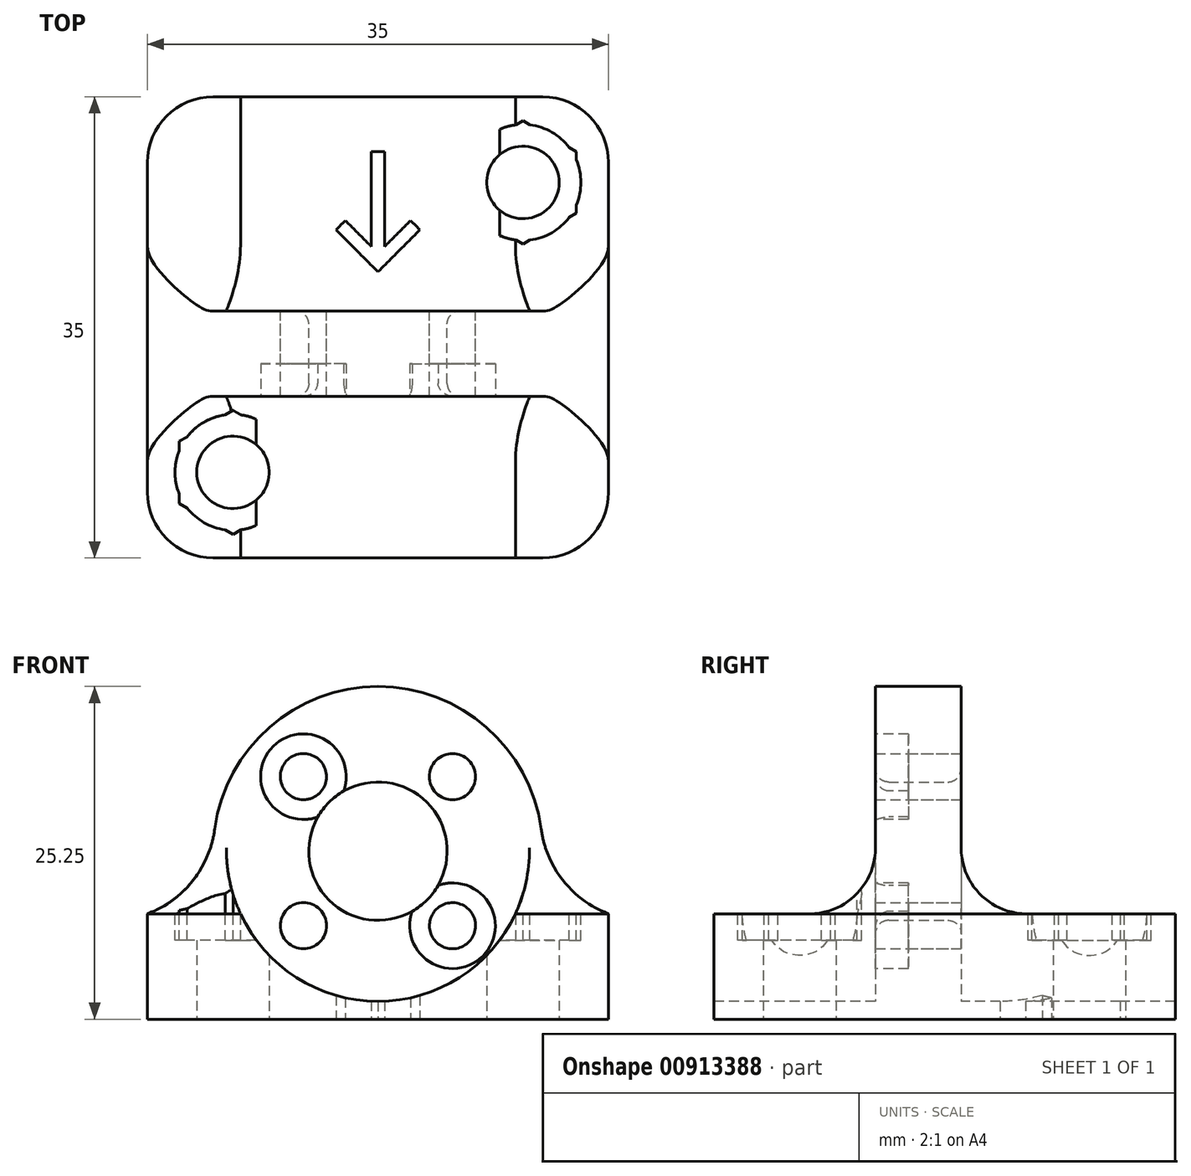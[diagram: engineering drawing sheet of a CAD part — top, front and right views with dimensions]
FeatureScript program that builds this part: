
annotation { "Feature Type Name" : "Feature", "Feature Type Description" : "" }
export const myFeature = defineFeature(function(context is Context, id is Id, definition is map)
    precondition{}
    {
        {
            var Q0;
            Q0=qCreatedBy(makeId("Front.planeOp"),FACE);
            cPlane(context, id + "F0", {"entities" : qUnion([Q0]), "cplaneType" : CPlaneType.OFFSET, "offset" : 2 * mm, "width" : 150 * mm, "height" : 150 * mm});
        }
        {
            var Q0;
            Q0=qCreatedBy(makeId("Top.planeOp"),FACE);
            var sketch = newSketch(context, id + "F1", { "sketchPlane" : qUnion([Q0])});
            skLineSegment(sketch, "E0.bottom", {"start": v(-17.5, 17.5) * mm, "end": v(17.5, 17.5) * mm});
            skLineSegment(sketch, "E0.top", {"start": v(-17.5, -17.5) * mm, "end": v(17.5, -17.5) * mm});
            skLineSegment(sketch, "E0.left", {"start": v(-17.5, 17.5) * mm, "end": v(-17.5, -17.5) * mm});
            skLineSegment(sketch, "E0.right", {"start": v(17.5, 17.5) * mm, "end": v(17.5, -17.5) * mm});
            skPoint(sketch, "E0.middle", {"position": v(0, 0) * mm});
            skLineSegment(sketch, "E1.bottom", {"start": v(-11, 11) * mm, "end": v(11, 11) * mm, "construction": true});
            skLineSegment(sketch, "E1.top", {"start": v(-11, -11) * mm, "end": v(11, -11) * mm, "construction": true});
            skLineSegment(sketch, "E1.left", {"start": v(-11, 11) * mm, "end": v(-11, -11) * mm, "construction": true});
            skLineSegment(sketch, "E1.right", {"start": v(11, 11) * mm, "end": v(11, -11) * mm, "construction": true});
            skCircle(sketch, "E2", {"center": v(-11, 11) * mm, "radius": 2.75 * mm, "construction": true});
            skCircle(sketch, "E3", {"center": v(11, 11) * mm, "radius": 2.75 * mm});
            skCircle(sketch, "E4", {"center": v(11, -11) * mm, "radius": 2.75 * mm, "construction": true});
            skCircle(sketch, "E5", {"center": v(-11, -11) * mm, "radius": 2.75 * mm});
            skSolve(sketch);
        }
        {
            var Q0;
            Q0=qSketchRegion(id+"F1",true);
            extrude(context, id + "F2", {"entities" : qUnion([Q0]), "depth" : 8 * mm, "offsetDistance" : 25 * mm});
        }
        {
            var Q0;
            Q0=qCreatedBy(id+"F0.planeOp",FACE);
            var sketch = newSketch(context, id + "F3", { "sketchPlane" : qUnion([Q0])});
            skLineSegment(sketch, "E6", {"start": v(0, 0) * mm, "end": v(0, 12.75) * mm, "construction": true});
            skArc(sketch, "E7", {"start": v(12.5, 12.75) * mm, "mid": v(0, 25.25) * mm, "end": v(-12.5, 12.75) * mm});
            skLineSegment(sketch, "E8", {"start": v(-12.5, 12.75) * mm, "end": v(-12.5, 0) * mm});
            skLineSegment(sketch, "E9.MirrorCS", {"start": v(12.5, 12.75) * mm, "end": v(12.5, 0) * mm});
            skCircle(sketch, "E10", {"center": v(0, 12.75) * mm, "radius": 5.25 * mm});
            skCircle(sketch, "E11", {"center": v(0, 12.75) * mm, "radius": 8 * mm, "construction": true});
            skLineSegment(sketch, "E12", {"start": v(0, 20.75) * mm, "end": v(0, 4.75) * mm, "construction": true});
            skPoint(sketch, "E12.startSnap0", {"position": v(0, 25.25) * mm});
            skLineSegment(sketch, "E13", {"start": v(-8, 12.75) * mm, "end": v(8, 12.75) * mm, "construction": true});
            skLineSegment(sketch, "E14", {"start": v(0, 12.75) * mm, "end": v(-5.66, 18.4) * mm, "construction": true});
            skLineSegment(sketch, "E15", {"start": v(0, 12.75) * mm, "end": v(-5.66, 7.1) * mm, "construction": true});
            skLineSegment(sketch, "E16.MirrorCS", {"start": v(0, 12.75) * mm, "end": v(5.66, 18.4) * mm, "construction": true});
            skLineSegment(sketch, "E17.MirrorCS", {"start": v(0, 12.75) * mm, "end": v(5.66, 7.1) * mm, "construction": true});
            skCircle(sketch, "E18", {"center": v(-5.66, 18.4) * mm, "radius": 1.75 * mm});
            skCircle(sketch, "E19", {"center": v(-5.66, 7.1) * mm, "radius": 1.75 * mm});
            skCircle(sketch, "E20", {"center": v(5.66, 7.1) * mm, "radius": 1.75 * mm});
            skCircle(sketch, "E21", {"center": v(5.66, 18.4) * mm, "radius": 1.75 * mm});
            skLineSegment(sketch, "E22", {"start": v(-12.5, 0) * mm, "end": v(12.5, 0) * mm});
            skSolve(sketch);
        }
        {
            var Q0;
            Q0=qCreatedBy(makeId("Front.planeOp"),FACE);
            var sketch = newSketch(context, id + "F4", { "sketchPlane" : qUnion([Q0])});
            skLineSegment(sketch, "E23", {"start": v(0, 0) * mm, "end": v(0, 12.85) * mm, "construction": true});
            skCircle(sketch, "E24", {"center": v(0, 12.85) * mm, "radius": 11.5 * mm});
            skSolve(sketch);
        }
        {
            var Q0;
            Q0=qSketchRegion(id+"F4",true);
            extrude(context, id + "F5", {"entities" : qUnion([Q0]), "operationType" : NewBodyOperationType.REMOVE, "oppositeDirection" : true, "depth" : 36 * mm, "offsetDistance" : 25 * mm, "symmetric" : true});
        }
        {
            var Q0;
            Q0=qSketchRegion(id+"F3",true);
            extrude(context, id + "F6", {"entities" : qUnion([Q0]), "operationType" : NewBodyOperationType.ADD, "depth" : 6.5 * mm, "offsetDistance" : 25 * mm, "symmetric" : true});
        }
        {
            var Q0;
            {var subQ0=sQuery(id+"F1.wireOp",EDGE,"E4");var subQ1=sQuery(id+"F1.wireOp",EDGE,"E0.top");var subQ2=sQuery(id+"F1.wireOp",EDGE,"E0.right");var subQ3=sQuery(id+"F1.wireOp",EDGE,"E0.bottom");Q0=makeQuery(id+"F6.boolean.opBoolean","INTERSECT",EDGE,{"derivedFrom":[makeQuery(id+"F5.boolean.opBoolean","SPLIT",FACE,{"disambiguationData":[TD([makeQuery(id+"F2.opExtrude","SWEPT_FACE",FACE,{"disambiguationData":[OSD([subQ2])]})])],"derivedFrom":makeQuery(id+"F2.opExtrude","CAP_FACE",FACE,{"disambiguationData":[OSD([subQ3,subQ1,sQuery(id+"F1.wireOp",EDGE,"E0.left"),subQ2,sQuery(id+"F1.wireOp",EDGE,"E2"),subQ0])],"isStart":false})}),makeQuery(id+"F6.opExtrude","SWEPT_FACE",FACE,{"disambiguationData":[OSD([sQuery(id+"F3.wireOp",EDGE,"E9.MirrorCS")])]})]});}
            var Q1;
            {var subQ0=sQuery(id+"F1.wireOp",EDGE,"E2");var subQ1=sQuery(id+"F1.wireOp",EDGE,"E0.left");var subQ2=sQuery(id+"F1.wireOp",EDGE,"E0.top");var subQ3=sQuery(id+"F1.wireOp",EDGE,"E0.bottom");Q1=makeQuery(id+"F6.boolean.opBoolean","INTERSECT",EDGE,{"derivedFrom":[makeQuery(id+"F5.boolean.opBoolean","SPLIT",FACE,{"disambiguationData":[TD([makeQuery(id+"F2.opExtrude","SWEPT_FACE",FACE,{"disambiguationData":[OSD([subQ1])]})])],"derivedFrom":makeQuery(id+"F2.opExtrude","CAP_FACE",FACE,{"disambiguationData":[OSD([subQ3,subQ2,subQ1,sQuery(id+"F1.wireOp",EDGE,"E0.right"),subQ0,sQuery(id+"F1.wireOp",EDGE,"E4")])],"isStart":false})}),makeQuery(id+"F6.opExtrude","SWEPT_FACE",FACE,{"disambiguationData":[OSD([sQuery(id+"F3.wireOp",EDGE,"E8")])]})]});}
            fillet(context, id + "F7", {"entities" : qUnion([Q0, Q1]), "radius" : 8 * mm, "tangentPropagation" : true, "allowEdgeOverflow" : false});
        }
        {
            var Q0;
            {var subQ0=sQuery(id+"F1.wireOp",EDGE,"E2");var subQ1=sQuery(id+"F1.wireOp",EDGE,"E0.left");var subQ2=sQuery(id+"F1.wireOp",EDGE,"E0.top");var subQ3=sQuery(id+"F1.wireOp",EDGE,"E0.bottom");Q0=makeQuery(id+"F7.opFillet","SPLIT",FACE,{"disambiguationData":[OD(0.0)],"derivedFrom":makeQuery(id+"F5.boolean.opBoolean","SPLIT",FACE,{"disambiguationData":[TD([makeQuery(id+"F2.opExtrude","SWEPT_FACE",FACE,{"disambiguationData":[OSD([subQ1])]})])],"derivedFrom":makeQuery(id+"F2.opExtrude","CAP_FACE",FACE,{"disambiguationData":[OSD([subQ3,subQ2,subQ1,sQuery(id+"F1.wireOp",EDGE,"E0.right"),subQ0,sQuery(id+"F1.wireOp",EDGE,"E4")])],"isStart":false})})});}
            var sketch = newSketch(context, id + "F8", { "sketchPlane" : qUnion([Q0])});
            skPoint(sketch, "E25.0.midPoint.positionSnap0", {"position": v(5.2, -11) * mm});
            skLineSegment(sketch, "E26", {"start": v(17.5, 17.5) * mm, "end": v(-17.5, -17.5) * mm, "construction": true});
            skCircle(sketch, "E27.cCircle", {"center": v(11, 11) * mm, "radius": 4.05 * mm, "construction": true});
            skLineSegment(sketch, "E27.0", {"start": v(15.05, 13.34) * mm, "end": v(15.05, 8.66) * mm});
            skLineSegment(sketch, "E27.1", {"start": v(15.05, 8.66) * mm, "end": v(11, 6.32) * mm});
            skLineSegment(sketch, "E27.2", {"start": v(11, 6.32) * mm, "end": v(6.95, 8.66) * mm});
            skLineSegment(sketch, "E27.3", {"start": v(6.95, 8.66) * mm, "end": v(6.95, 13.34) * mm});
            skLineSegment(sketch, "E27.4", {"start": v(6.95, 13.34) * mm, "end": v(11, 15.68) * mm});
            skLineSegment(sketch, "E27.5", {"start": v(11, 15.68) * mm, "end": v(15.05, 13.34) * mm});
            skPoint(sketch, "E27.0.midPoint", {"position": v(15.05, 11) * mm});
            skCircle(sketch, "E28.cCircle", {"center": v(-11, -11) * mm, "radius": 4.08 * mm, "construction": true});
            skLineSegment(sketch, "E28.0", {"start": v(-11, -6.3) * mm, "end": v(-6.93, -8.65) * mm});
            skLineSegment(sketch, "E28.1", {"start": v(-6.93, -8.65) * mm, "end": v(-6.93, -13.35) * mm});
            skLineSegment(sketch, "E28.2", {"start": v(-6.93, -13.35) * mm, "end": v(-11, -15.7) * mm});
            skLineSegment(sketch, "E28.3", {"start": v(-11, -15.7) * mm, "end": v(-15.08, -13.35) * mm});
            skLineSegment(sketch, "E28.4", {"start": v(-15.07, -13.35) * mm, "end": v(-15.07, -8.65) * mm});
            skLineSegment(sketch, "E28.5", {"start": v(-15.07, -8.65) * mm, "end": v(-11, -6.3) * mm});
            skPoint(sketch, "E28.0.midPoint", {"position": v(-8.96, -7.47) * mm});
            skSolve(sketch);
        }
        {
            var Q0;
            Q0=qSketchRegion(id+"F8",true);
            extrude(context, id + "F9", {"entities" : qUnion([Q0]), "operationType" : NewBodyOperationType.REMOVE, "oppositeDirection" : true, "depth" : 2 * mm, "offsetDistance" : 25 * mm});
        }
        {
            var Q0;
            {var subQ0=sQuery(id+"F1.wireOp",EDGE,"E2");var subQ1=sQuery(id+"F1.wireOp",EDGE,"E0.left");var subQ2=sQuery(id+"F1.wireOp",EDGE,"E0.top");var subQ3=sQuery(id+"F1.wireOp",EDGE,"E0.bottom");Q0=makeQuery(id+"F7.opFillet","SPLIT",FACE,{"disambiguationData":[OD(0.0)],"derivedFrom":makeQuery(id+"F5.boolean.opBoolean","SPLIT",FACE,{"disambiguationData":[TD([makeQuery(id+"F2.opExtrude","SWEPT_FACE",FACE,{"disambiguationData":[OSD([subQ1])]})])],"derivedFrom":makeQuery(id+"F2.opExtrude","CAP_FACE",FACE,{"disambiguationData":[OSD([subQ3,subQ2,subQ1,sQuery(id+"F1.wireOp",EDGE,"E0.right"),subQ0,sQuery(id+"F1.wireOp",EDGE,"E4")])],"isStart":false})})});}
            var sketch = newSketch(context, id + "F10", { "sketchPlane" : qUnion([Q0])});
            skCircle(sketch, "E29", {"center": v(11, 11) * mm, "radius": 4.4 * mm});
            skCircle(sketch, "E30", {"center": v(-11, -11) * mm, "radius": 4.4 * mm});
            skSolve(sketch);
        }
        {
            var Q0;
            Q0=qSketchRegion(id+"F10",true);
            extrude(context, id + "F11", {"entities" : qUnion([Q0]), "operationType" : NewBodyOperationType.REMOVE, "oppositeDirection" : true, "depth" : 2 * mm, "offsetDistance" : 25 * mm});
        }
        {
            var Q0;
            {var subQ0=sQuery(id+"F1.wireOp",EDGE,"E4");var subQ1=sQuery(id+"F1.wireOp",EDGE,"E0.top");var subQ2=sQuery(id+"F1.wireOp",EDGE,"E0.right");var subQ3=sQuery(id+"F1.wireOp",EDGE,"E0.bottom");Q0=makeQuery(id+"F6.boolean.opBoolean","INTERSECT",EDGE,{"derivedFrom":[makeQuery(id+"F5.boolean.opBoolean","SPLIT",FACE,{"disambiguationData":[TD([makeQuery(id+"F2.opExtrude","SWEPT_FACE",FACE,{"disambiguationData":[OSD([subQ2])]})])],"derivedFrom":makeQuery(id+"F2.opExtrude","CAP_FACE",FACE,{"disambiguationData":[OSD([subQ3,subQ1,sQuery(id+"F1.wireOp",EDGE,"E0.left"),subQ2,sQuery(id+"F1.wireOp",EDGE,"E2"),subQ0])],"isStart":false})}),makeQuery(id+"F6.opExtrude","CAP_FACE",FACE,{"disambiguationData":[OSD([sQuery(id+"F3.wireOp",EDGE,"E7"),sQuery(id+"F3.wireOp",EDGE,"E8"),sQuery(id+"F3.wireOp",EDGE,"E9.MirrorCS"),sQuery(id+"F3.wireOp",EDGE,"E10"),sQuery(id+"F3.wireOp",EDGE,"E18"),sQuery(id+"F3.wireOp",EDGE,"E19"),sQuery(id+"F3.wireOp",EDGE,"E20"),sQuery(id+"F3.wireOp",EDGE,"E21"),sQuery(id+"F3.wireOp",EDGE,"E22")])],"isStart":true})]});}
            var Q1;
            {var subQ0=sQuery(id+"F1.wireOp",EDGE,"E2");var subQ1=sQuery(id+"F1.wireOp",EDGE,"E0.left");var subQ2=sQuery(id+"F1.wireOp",EDGE,"E0.top");var subQ3=sQuery(id+"F1.wireOp",EDGE,"E0.bottom");Q1=makeQuery(id+"F6.boolean.opBoolean","INTERSECT",EDGE,{"derivedFrom":[makeQuery(id+"F5.boolean.opBoolean","SPLIT",FACE,{"disambiguationData":[TD([makeQuery(id+"F2.opExtrude","SWEPT_FACE",FACE,{"disambiguationData":[OSD([subQ1])]})])],"derivedFrom":makeQuery(id+"F2.opExtrude","CAP_FACE",FACE,{"disambiguationData":[OSD([subQ3,subQ2,subQ1,sQuery(id+"F1.wireOp",EDGE,"E0.right"),subQ0,sQuery(id+"F1.wireOp",EDGE,"E4")])],"isStart":false})}),makeQuery(id+"F6.opExtrude","CAP_FACE",FACE,{"disambiguationData":[OSD([sQuery(id+"F3.wireOp",EDGE,"E7"),sQuery(id+"F3.wireOp",EDGE,"E8"),sQuery(id+"F3.wireOp",EDGE,"E9.MirrorCS"),sQuery(id+"F3.wireOp",EDGE,"E10"),sQuery(id+"F3.wireOp",EDGE,"E18"),sQuery(id+"F3.wireOp",EDGE,"E19"),sQuery(id+"F3.wireOp",EDGE,"E20"),sQuery(id+"F3.wireOp",EDGE,"E21"),sQuery(id+"F3.wireOp",EDGE,"E22")])],"isStart":true})]});}
            var Q2;
            {var subQ0=sQuery(id+"F1.wireOp",EDGE,"E2");var subQ1=sQuery(id+"F1.wireOp",EDGE,"E0.left");var subQ2=sQuery(id+"F1.wireOp",EDGE,"E0.top");var subQ3=sQuery(id+"F1.wireOp",EDGE,"E0.bottom");Q2=makeQuery(id+"F6.boolean.opBoolean","INTERSECT",EDGE,{"derivedFrom":[makeQuery(id+"F5.boolean.opBoolean","SPLIT",FACE,{"disambiguationData":[TD([makeQuery(id+"F2.opExtrude","SWEPT_FACE",FACE,{"disambiguationData":[OSD([subQ1])]})])],"derivedFrom":makeQuery(id+"F2.opExtrude","CAP_FACE",FACE,{"disambiguationData":[OSD([subQ3,subQ2,subQ1,sQuery(id+"F1.wireOp",EDGE,"E0.right"),subQ0,sQuery(id+"F1.wireOp",EDGE,"E4")])],"isStart":false})}),makeQuery(id+"F6.opExtrude","CAP_FACE",FACE,{"disambiguationData":[OSD([sQuery(id+"F3.wireOp",EDGE,"E7"),sQuery(id+"F3.wireOp",EDGE,"E8"),sQuery(id+"F3.wireOp",EDGE,"E9.MirrorCS"),sQuery(id+"F3.wireOp",EDGE,"E10"),sQuery(id+"F3.wireOp",EDGE,"E18"),sQuery(id+"F3.wireOp",EDGE,"E19"),sQuery(id+"F3.wireOp",EDGE,"E20"),sQuery(id+"F3.wireOp",EDGE,"E21"),sQuery(id+"F3.wireOp",EDGE,"E22")])],"isStart":false})]});}
            var Q3;
            {var subQ0=sQuery(id+"F1.wireOp",EDGE,"E4");var subQ1=sQuery(id+"F1.wireOp",EDGE,"E0.top");var subQ2=sQuery(id+"F1.wireOp",EDGE,"E0.right");var subQ3=sQuery(id+"F1.wireOp",EDGE,"E0.bottom");Q3=makeQuery(id+"F6.boolean.opBoolean","INTERSECT",EDGE,{"derivedFrom":[makeQuery(id+"F5.boolean.opBoolean","SPLIT",FACE,{"disambiguationData":[TD([makeQuery(id+"F2.opExtrude","SWEPT_FACE",FACE,{"disambiguationData":[OSD([subQ2])]})])],"derivedFrom":makeQuery(id+"F2.opExtrude","CAP_FACE",FACE,{"disambiguationData":[OSD([subQ3,subQ1,sQuery(id+"F1.wireOp",EDGE,"E0.left"),subQ2,sQuery(id+"F1.wireOp",EDGE,"E2"),subQ0])],"isStart":false})}),makeQuery(id+"F6.opExtrude","CAP_FACE",FACE,{"disambiguationData":[OSD([sQuery(id+"F3.wireOp",EDGE,"E7"),sQuery(id+"F3.wireOp",EDGE,"E8"),sQuery(id+"F3.wireOp",EDGE,"E9.MirrorCS"),sQuery(id+"F3.wireOp",EDGE,"E10"),sQuery(id+"F3.wireOp",EDGE,"E18"),sQuery(id+"F3.wireOp",EDGE,"E19"),sQuery(id+"F3.wireOp",EDGE,"E20"),sQuery(id+"F3.wireOp",EDGE,"E21"),sQuery(id+"F3.wireOp",EDGE,"E22")])],"isStart":false})]});}
            var Q4;
            Q4=makeQuery(id+"F2.opExtrude","SWEPT_EDGE",EDGE,{"disambiguationData":[OSD([sQuery(id+"F1.wireOp",EDGE,"E0.top"),sQuery(id+"F1.wireOp",EDGE,"E0.left")])]});
            var Q5;
            Q5=makeQuery(id+"F2.opExtrude","SWEPT_EDGE",EDGE,{"disambiguationData":[OSD([sQuery(id+"F1.wireOp",EDGE,"E0.bottom"),sQuery(id+"F1.wireOp",EDGE,"E0.left")])]});
            var Q6;
            Q6=makeQuery(id+"F2.opExtrude","SWEPT_EDGE",EDGE,{"disambiguationData":[OSD([sQuery(id+"F1.wireOp",EDGE,"E0.bottom"),sQuery(id+"F1.wireOp",EDGE,"E0.right")])]});
            var Q7;
            Q7=makeQuery(id+"F2.opExtrude","SWEPT_EDGE",EDGE,{"disambiguationData":[OSD([sQuery(id+"F1.wireOp",EDGE,"E0.top"),sQuery(id+"F1.wireOp",EDGE,"E0.right")])]});
            fillet(context, id + "F12", {"entities" : qUnion([Q0, Q1, Q2, Q3, Q4, Q5, Q6, Q7]), "radius" : 5 * mm, "tangentPropagation" : true, "allowEdgeOverflow" : false});
        }
        {
            var Q0;
            Q0=makeQuery(id+"F6.opExtrude","CAP_FACE",FACE,{"disambiguationData":[OSD([sQuery(id+"F3.wireOp",EDGE,"E7"),sQuery(id+"F3.wireOp",EDGE,"E8"),sQuery(id+"F3.wireOp",EDGE,"E9.MirrorCS"),sQuery(id+"F3.wireOp",EDGE,"E10"),sQuery(id+"F3.wireOp",EDGE,"E18"),sQuery(id+"F3.wireOp",EDGE,"E20"),sQuery(id+"F3.wireOp",EDGE,"E22")])],"isStart":false});
            var sketch = newSketch(context, id + "F13", { "sketchPlane" : qUnion([Q0])});
            skCircle(sketch, "E31", {"center": v(-5.66, 18.4) * mm, "radius": 3.25 * mm});
            skCircle(sketch, "E32", {"center": v(5.66, 7.1) * mm, "radius": 3.25 * mm});
            skLineSegment(sketch, "E33", {"start": v(0, 12.75) * mm, "end": v(12.71, 12.75) * mm, "construction": true});
            skCircle(sketch, "E34.MirrorC", {"center": v(5.66, 18.4) * mm, "radius": 3.25 * mm});
            skCircle(sketch, "E35.MirrorC", {"center": v(-5.66, 7.1) * mm, "radius": 3.25 * mm});
            skSolve(sketch);
        }
        {
            var Q0;
            Q0=makeQuery(id+"F13.imprint","IMPRINT",FACE,{"disambiguationData":[TD([[makeQuery(id+"F13.imprint","IMPRINT",EDGE,{"derivedFrom":sQuery(id+"F13.wireOp",EDGE,"E31")}),1.0]])]});
            var Q1;
            Q1=makeQuery(id+"F13.imprint","IMPRINT",FACE,{"disambiguationData":[TD([[makeQuery(id+"F13.imprint","IMPRINT",EDGE,{"derivedFrom":sQuery(id+"F13.wireOp",EDGE,"E32")}),1.0]])]});
            var Q2;
            Q2=makeQuery(id+"F13.imprint","IMPRINT",FACE,{"disambiguationData":[TD([[makeQuery(id+"F13.imprint","IMPRINT",EDGE,{"derivedFrom":makeQuery(id+"F6.opExtrude","CAP_EDGE",EDGE,{"disambiguationData":[OSD([sQuery(id+"F3.wireOp",EDGE,"E18")])],"isStart":false})}),-1.0]])]});
            var Q3;
            Q3=makeQuery(id+"F13.imprint","IMPRINT",FACE,{"disambiguationData":[TD([[makeQuery(id+"F13.imprint","IMPRINT",EDGE,{"derivedFrom":makeQuery(id+"F6.opExtrude","CAP_EDGE",EDGE,{"disambiguationData":[OSD([sQuery(id+"F3.wireOp",EDGE,"E20")])],"isStart":false})}),-1.0]])]});
            var Q4;
            {var subQ0=sQuery(id+"F13.wireOp",EDGE,"E34.MirrorC");var subQ1=makeQuery(id+"F6.opExtrude","CAP_EDGE",EDGE,{"disambiguationData":[OSD([sQuery(id+"F3.wireOp",EDGE,"E10")])],"isStart":false});var subQ2=makeQuery(id+"F13.imprint","INTERSECT",VERTEX,{"disambiguationData":[OD(0.0)],"derivedFrom":[subQ1,subQ0]});Q4=makeQuery(id+"F13.imprint","IMPRINT",FACE,{"disambiguationData":[TD([[makeQuery(id+"F13.imprint","IMPRINT",EDGE,{"disambiguationData":[TD([[subQ2,-1.0]])],"derivedFrom":subQ0}),-1.0]])]});}
            var Q5;
            {var subQ0=sQuery(id+"F13.wireOp",EDGE,"E35.MirrorC");var subQ1=makeQuery(id+"F6.opExtrude","CAP_EDGE",EDGE,{"disambiguationData":[OSD([sQuery(id+"F3.wireOp",EDGE,"E10")])],"isStart":false});var subQ2=makeQuery(id+"F13.imprint","INTERSECT",VERTEX,{"disambiguationData":[OD(0.0)],"derivedFrom":[subQ1,subQ0]});Q5=makeQuery(id+"F13.imprint","IMPRINT",FACE,{"disambiguationData":[TD([[makeQuery(id+"F13.imprint","IMPRINT",EDGE,{"disambiguationData":[TD([[subQ2,1.0]])],"derivedFrom":subQ0}),-1.0]])]});}
            var Q6;
            Q6=makeQuery(id+"F6.opExtrude","CAP_FACE",FACE,{"disambiguationData":[OSD([sQuery(id+"F3.wireOp",EDGE,"E7"),sQuery(id+"F3.wireOp",EDGE,"E8"),sQuery(id+"F3.wireOp",EDGE,"E9.MirrorCS"),sQuery(id+"F3.wireOp",EDGE,"E10"),sQuery(id+"F3.wireOp",EDGE,"E18"),sQuery(id+"F3.wireOp",EDGE,"E20"),sQuery(id+"F3.wireOp",EDGE,"E22")])],"isStart":true});
            extrude(context, id + "F14", {"entities" : qUnion([Q0, Q1, Q2, Q3, Q4, Q5]), "operationType" : NewBodyOperationType.REMOVE, "oppositeDirection" : true, "depth" : 2.5 * mm, "endBoundEntityFace" : qUnion([Q6]), "hasOffset" : true, "offsetDistance" : 5 * mm, "offsetOppositeDirection" : true});
        }
        {
            var Q0;
            Q0=makeQuery(id+"F2.opExtrude","CAP_FACE",FACE,{"disambiguationData":[OSD([sQuery(id+"F1.wireOp",EDGE,"E0.bottom"),sQuery(id+"F1.wireOp",EDGE,"E0.top"),sQuery(id+"F1.wireOp",EDGE,"E0.left"),sQuery(id+"F1.wireOp",EDGE,"E0.right"),sQuery(id+"F1.wireOp",EDGE,"E3"),sQuery(id+"F1.wireOp",EDGE,"E5")])],"isStart":true});
            var sketch = newSketch(context, id + "F15", { "sketchPlane" : qUnion([Q0])});
            skLineSegment(sketch, "E36", {"start": v(0, 0) * mm, "end": v(0, -17.5) * mm, "construction": true});
            skLineSegment(sketch, "E37", {"start": v(0, -4.22) * mm, "end": v(-3.18, -7.4) * mm});
            skLineSegment(sketch, "E38", {"start": v(-3.18, -7.4) * mm, "end": v(-2.47, -8.1) * mm});
            skLineSegment(sketch, "E39", {"start": v(-2.47, -8.1) * mm, "end": v(-0.5, -6.13) * mm});
            skLineSegment(sketch, "E40", {"start": v(-0.5, -6.13) * mm, "end": v(-0.5, -13.33) * mm});
            skLineSegment(sketch, "E41", {"start": v(-0.5, -13.33) * mm, "end": v(0, -13.33) * mm});
            skLineSegment(sketch, "E42.MirrorCS", {"start": v(0.5, -13.33) * mm, "end": v(0, -13.33) * mm});
            skLineSegment(sketch, "E43.MirrorCS", {"start": v(3.18, -7.4) * mm, "end": v(2.47, -8.1) * mm});
            skLineSegment(sketch, "E44.MirrorCS", {"start": v(0.5, -6.13) * mm, "end": v(0.5, -13.33) * mm});
            skLineSegment(sketch, "E45.MirrorCS", {"start": v(2.47, -8.1) * mm, "end": v(0.5, -6.13) * mm});
            skLineSegment(sketch, "E46.MirrorCS", {"start": v(0, -4.22) * mm, "end": v(3.18, -7.4) * mm});
            skSolve(sketch);
        }
        {
            var Q0;
            Q0=qSketchRegion(id+"F15",true);
            extrude(context, id + "F16", {"entities" : qUnion([Q0]), "operationType" : NewBodyOperationType.REMOVE, "oppositeDirection" : true, "depth" : 3 * mm, "offsetDistance" : 25 * mm});
        }
        {
            var Q0;
            Q0=makeQuery(id+"F14.boolean.opBoolean","COPY",EDGE,{"derivedFrom":makeQuery(id+"F14.opExtrude","CAP_EDGE",EDGE,{"disambiguationData":[OSD([sQuery(id+"F13.wireOp",EDGE,"E31")])],"isStart":true})});
            var Q1;
            Q1=makeQuery(id+"F14.boolean.opBoolean","COPY",EDGE,{"derivedFrom":makeQuery(id+"F14.opExtrude","CAP_EDGE",EDGE,{"disambiguationData":[OSD([sQuery(id+"F13.wireOp",EDGE,"E34.MirrorC")])],"isStart":true})});
            var Q2;
            Q2=makeQuery(id+"F14.boolean.opBoolean","COPY",EDGE,{"derivedFrom":makeQuery(id+"F14.opExtrude","CAP_EDGE",EDGE,{"disambiguationData":[OSD([sQuery(id+"F13.wireOp",EDGE,"E32")])],"isStart":true})});
            var Q3;
            Q3=makeQuery(id+"F14.boolean.opBoolean","COPY",EDGE,{"derivedFrom":makeQuery(id+"F14.opExtrude","CAP_EDGE",EDGE,{"disambiguationData":[OSD([sQuery(id+"F13.wireOp",EDGE,"E35.MirrorC")])],"isStart":true})});
            var Q4;
            {var subQ0=sQuery(id+"F3.wireOp",EDGE,"E10");Q4=makeQuery(id+"F14.boolean.opBoolean","SPLIT",EDGE,{"disambiguationData":[TD([makeQuery(id+"F6.opExtrude","CAP_FACE",FACE,{"disambiguationData":[OSD([sQuery(id+"F3.wireOp",EDGE,"E7"),sQuery(id+"F3.wireOp",EDGE,"E8"),sQuery(id+"F3.wireOp",EDGE,"E9.MirrorCS"),subQ0,sQuery(id+"F3.wireOp",EDGE,"E18"),sQuery(id+"F3.wireOp",EDGE,"E19"),sQuery(id+"F3.wireOp",EDGE,"E20"),sQuery(id+"F3.wireOp",EDGE,"E21"),sQuery(id+"F3.wireOp",EDGE,"E22")])],"isStart":false}),makeQuery(id+"F6.opExtrude","SWEPT_FACE",FACE,{"disambiguationData":[OSD([subQ0])]}),makeQuery(id+"F14.opExtrude","SWEPT_FACE",FACE,{"disambiguationData":[OSD([sQuery(id+"F13.wireOp",EDGE,"E31")])]}),makeQuery(id+"F14.opExtrude","SWEPT_FACE",FACE,{"disambiguationData":[OSD([sQuery(id+"F13.wireOp",EDGE,"E35.MirrorC")])]})])],"derivedFrom":makeQuery(id+"F6.opExtrude","CAP_EDGE",EDGE,{"disambiguationData":[OSD([subQ0])],"isStart":false})});}
            var Q5;
            {var subQ0=sQuery(id+"F3.wireOp",EDGE,"E10");Q5=makeQuery(id+"F14.boolean.opBoolean","SPLIT",EDGE,{"disambiguationData":[TD([makeQuery(id+"F6.opExtrude","CAP_FACE",FACE,{"disambiguationData":[OSD([sQuery(id+"F3.wireOp",EDGE,"E7"),sQuery(id+"F3.wireOp",EDGE,"E8"),sQuery(id+"F3.wireOp",EDGE,"E9.MirrorCS"),subQ0,sQuery(id+"F3.wireOp",EDGE,"E18"),sQuery(id+"F3.wireOp",EDGE,"E19"),sQuery(id+"F3.wireOp",EDGE,"E20"),sQuery(id+"F3.wireOp",EDGE,"E21"),sQuery(id+"F3.wireOp",EDGE,"E22")])],"isStart":false}),makeQuery(id+"F6.opExtrude","SWEPT_FACE",FACE,{"disambiguationData":[OSD([subQ0])]}),makeQuery(id+"F14.opExtrude","SWEPT_FACE",FACE,{"disambiguationData":[OSD([sQuery(id+"F13.wireOp",EDGE,"E31")])]}),makeQuery(id+"F14.opExtrude","SWEPT_FACE",FACE,{"disambiguationData":[OSD([sQuery(id+"F13.wireOp",EDGE,"E34.MirrorC")])]})])],"derivedFrom":makeQuery(id+"F6.opExtrude","CAP_EDGE",EDGE,{"disambiguationData":[OSD([subQ0])],"isStart":false})});}
            var Q6;
            {var subQ0=sQuery(id+"F3.wireOp",EDGE,"E10");Q6=makeQuery(id+"F14.boolean.opBoolean","SPLIT",EDGE,{"disambiguationData":[TD([makeQuery(id+"F6.opExtrude","CAP_FACE",FACE,{"disambiguationData":[OSD([sQuery(id+"F3.wireOp",EDGE,"E7"),sQuery(id+"F3.wireOp",EDGE,"E8"),sQuery(id+"F3.wireOp",EDGE,"E9.MirrorCS"),subQ0,sQuery(id+"F3.wireOp",EDGE,"E18"),sQuery(id+"F3.wireOp",EDGE,"E19"),sQuery(id+"F3.wireOp",EDGE,"E20"),sQuery(id+"F3.wireOp",EDGE,"E21"),sQuery(id+"F3.wireOp",EDGE,"E22")])],"isStart":false}),makeQuery(id+"F6.opExtrude","SWEPT_FACE",FACE,{"disambiguationData":[OSD([subQ0])]}),makeQuery(id+"F14.opExtrude","SWEPT_FACE",FACE,{"disambiguationData":[OSD([sQuery(id+"F13.wireOp",EDGE,"E32")])]}),makeQuery(id+"F14.opExtrude","SWEPT_FACE",FACE,{"disambiguationData":[OSD([sQuery(id+"F13.wireOp",EDGE,"E34.MirrorC")])]})])],"derivedFrom":makeQuery(id+"F6.opExtrude","CAP_EDGE",EDGE,{"disambiguationData":[OSD([subQ0])],"isStart":false})});}
            var Q7;
            {var subQ0=sQuery(id+"F3.wireOp",EDGE,"E10");Q7=makeQuery(id+"F14.boolean.opBoolean","SPLIT",EDGE,{"disambiguationData":[TD([makeQuery(id+"F6.opExtrude","CAP_FACE",FACE,{"disambiguationData":[OSD([sQuery(id+"F3.wireOp",EDGE,"E7"),sQuery(id+"F3.wireOp",EDGE,"E8"),sQuery(id+"F3.wireOp",EDGE,"E9.MirrorCS"),subQ0,sQuery(id+"F3.wireOp",EDGE,"E18"),sQuery(id+"F3.wireOp",EDGE,"E19"),sQuery(id+"F3.wireOp",EDGE,"E20"),sQuery(id+"F3.wireOp",EDGE,"E21"),sQuery(id+"F3.wireOp",EDGE,"E22")])],"isStart":false}),makeQuery(id+"F6.opExtrude","SWEPT_FACE",FACE,{"disambiguationData":[OSD([subQ0])]}),makeQuery(id+"F14.opExtrude","SWEPT_FACE",FACE,{"disambiguationData":[OSD([sQuery(id+"F13.wireOp",EDGE,"E32")])]}),makeQuery(id+"F14.opExtrude","SWEPT_FACE",FACE,{"disambiguationData":[OSD([sQuery(id+"F13.wireOp",EDGE,"E35.MirrorC")])]})])],"derivedFrom":makeQuery(id+"F6.opExtrude","CAP_EDGE",EDGE,{"disambiguationData":[OSD([subQ0])],"isStart":false})});}
            var Q8;
            Q8=makeQuery(id+"F6.opExtrude","CAP_EDGE",EDGE,{"disambiguationData":[OSD([sQuery(id+"F3.wireOp",EDGE,"E10")])],"isStart":true});
            fillet(context, id + "F17", {"entities" : qUnion([Q0, Q1, Q2, Q3, Q4, Q5, Q6, Q7, Q8]), "radius" : 1 * mm, "tangentPropagation" : true, "allowEdgeOverflow" : false});
        }
    });
